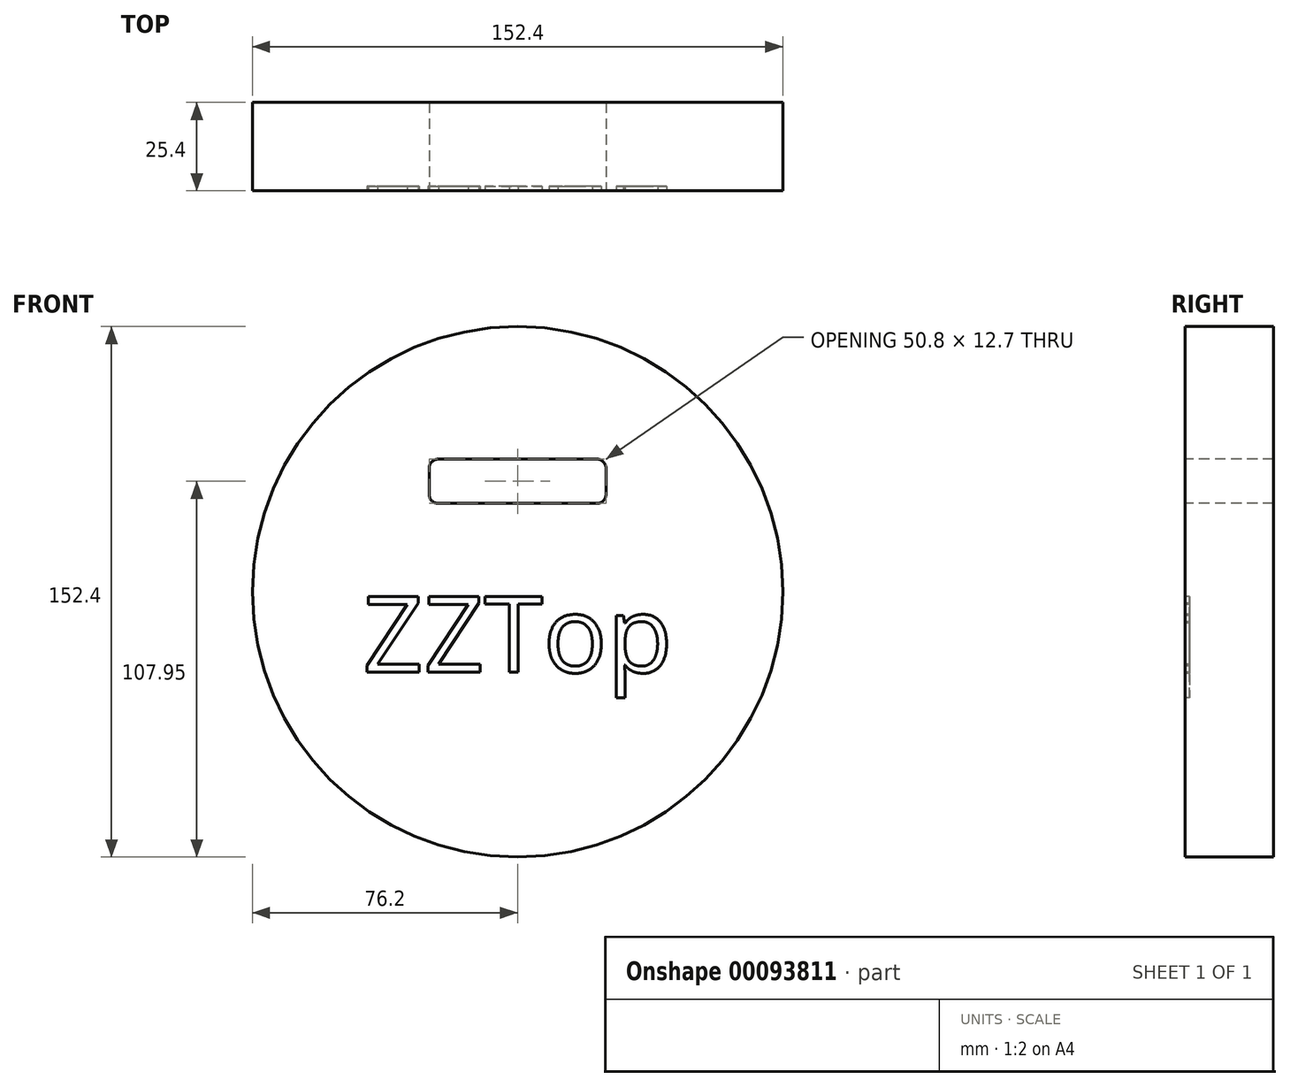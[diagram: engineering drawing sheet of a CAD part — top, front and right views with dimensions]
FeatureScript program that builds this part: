
annotation { "Feature Type Name" : "Feature", "Feature Type Description" : "" }
export const myFeature = defineFeature(function(context is Context, id is Id, definition is map)
    precondition{}
    {
        {
            var Q0;
            Q0=qCreatedBy(makeId("Front.planeOp"),FACE);
            var sketch = newSketch(context, id + "F0", { "sketchPlane" : qUnion([Q0])});
            skCircle(sketch, "E0", {"center": v(0, 0) * mm, "radius": 76.2 * mm});
            skSolve(sketch);
        }
        {
            var Q0;
            Q0=makeQuery(id+"F0.imprint","IMPRINT",FACE,{"disambiguationData":[TD([[makeQuery(id+"F0.imprint","IMPRINT",EDGE,{"derivedFrom":sQuery(id+"F0.wireOp",EDGE,"E0")}),1.0]])]});
            extrude(context, id + "F1", {"entities" : qUnion([Q0]), "endBound" : BoundingType.SYMMETRIC, "depth" : 25.4 * mm});
        }
        {
            var Q0;
            Q0=makeQuery(id+"F1.opExtrude","CAP_FACE",FACE,{"disambiguationData":[OSD([sQuery(id+"F0.wireOp",EDGE,"E0")])],"isStart":false});
            var sketch = newSketch(context, id + "F2", { "sketchPlane" : qUnion([Q0])});
            skLineSegment(sketch, "E1.bottom", {"start": v(-25.4, 38.1) * mm, "end": v(25.4, 38.1) * mm});
            skLineSegment(sketch, "E1.top", {"start": v(-25.4, 25.4) * mm, "end": v(25.4, 25.4) * mm});
            skLineSegment(sketch, "E1.left", {"start": v(-25.4, 38.1) * mm, "end": v(-25.4, 25.4) * mm});
            skLineSegment(sketch, "E2", {"start": v(0, 0) * mm, "end": v(0, 84.89) * mm, "construction": true});
            skLineSegment(sketch, "E3.MirrorCS", {"start": v(25.4, 38.1) * mm, "end": v(25.4, 25.4) * mm});
            skSolve(sketch);
        }
        {
            var Q0;
            Q0 = qSketchRegion(id + "F2", true);
            extrude(context, id + "F3", {"entities" : qUnion([Q0]), "operationType" : NewBodyOperationType.REMOVE, "endBound" : BoundingType.THROUGH_ALL, "oppositeDirection" : true, "depth" : 25.4 * mm});
        }
        {
            var Q0;
            Q0=makeQuery(id+"F3.boolean.opBoolean","COPY",EDGE,{"derivedFrom":makeQuery(id+"F3.opExtrude","SWEPT_EDGE",EDGE,{"disambiguationData":[OSD([sQuery(id+"F2.wireOp",EDGE,"E1.top"),sQuery(id+"F2.wireOp",EDGE,"E1.left")])]})});
            var Q1;
            Q1=makeQuery(id+"F3.boolean.opBoolean","COPY",EDGE,{"derivedFrom":makeQuery(id+"F3.opExtrude","SWEPT_EDGE",EDGE,{"disambiguationData":[OSD([sQuery(id+"F2.wireOp",EDGE,"E1.bottom"),sQuery(id+"F2.wireOp",EDGE,"E1.left")])]})});
            var Q2;
            Q2=makeQuery(id+"F3.boolean.opBoolean","COPY",EDGE,{"derivedFrom":makeQuery(id+"F3.opExtrude","SWEPT_EDGE",EDGE,{"disambiguationData":[OSD([sQuery(id+"F2.wireOp",EDGE,"E1.bottom"),sQuery(id+"F2.wireOp",EDGE,"E3.MirrorCS")])]})});
            var Q3;
            Q3=makeQuery(id+"F3.boolean.opBoolean","COPY",EDGE,{"derivedFrom":makeQuery(id+"F3.opExtrude","SWEPT_EDGE",EDGE,{"disambiguationData":[OSD([sQuery(id+"F2.wireOp",EDGE,"E1.top"),sQuery(id+"F2.wireOp",EDGE,"E3.MirrorCS")])]})});
            fillet(context, id + "F4", {"entities" : qUnion([Q0, Q1, Q2, Q3]), "radius" : 2.54 * mm, "tangentPropagation" : true, "allowEdgeOverflow" : false});
        }
        {
            var Q0;
            Q0=makeQuery(id+"F2.imprint","IMPRINT",FACE,{"disambiguationData":[TD([[makeQuery(id+"F2.imprint","IMPRINT",EDGE,{"derivedFrom":sQuery(id+"F2.wireOp",EDGE,"E1.bottom")}),1.0]])]});
            var sketch = newSketch(context, id + "F5", { "sketchPlane" : qUnion([Q0])});
            skText(sketch, "E4", { "text": "ZZTop", "fontName": "OpenSans-Regular.ttf"});
            const initialGuessF5  = {"E4": [-0.04447, -0.02312, 1, 0, 0.022]};
            skSetInitialGuess(sketch, initialGuessF5);
            skSolve(sketch);
        }
        {
            var Q0;
            Q0 = qSketchRegion(id + "F5", true);
            extrude(context, id + "F6", {"entities" : qUnion([Q0]), "operationType" : NewBodyOperationType.REMOVE, "oppositeDirection" : true, "depth" : 1.27 * mm});
        }
    });
